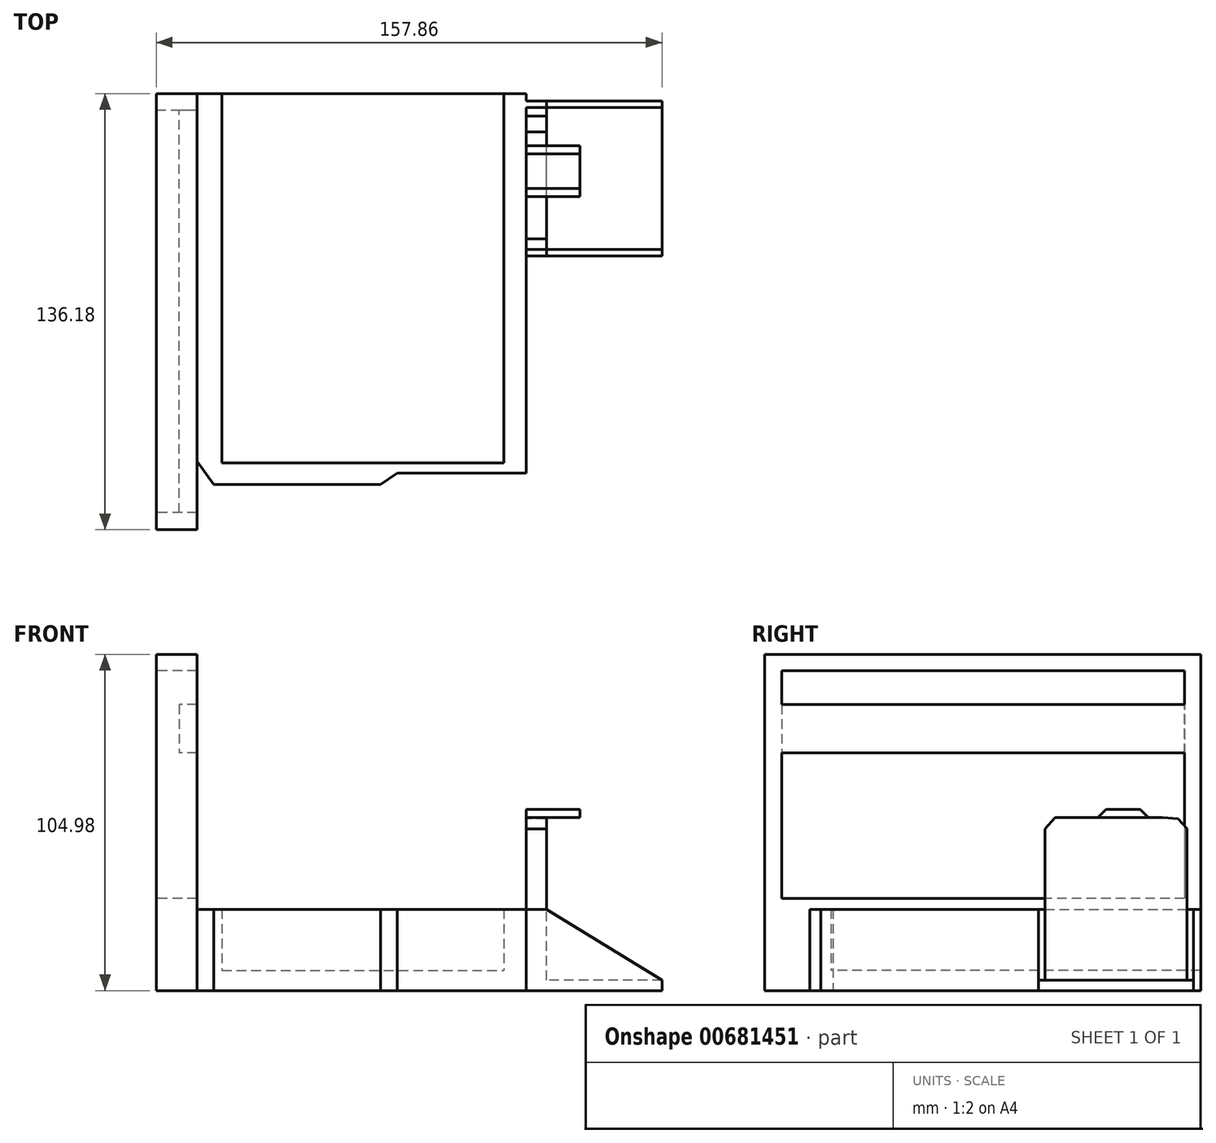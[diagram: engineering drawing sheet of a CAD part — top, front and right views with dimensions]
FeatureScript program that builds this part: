
annotation { "Feature Type Name" : "Feature", "Feature Type Description" : "" }
export const myFeature = defineFeature(function(context is Context, id is Id, definition is map)
    precondition{}
    {
        {
            var Q0;
            Q0=qCreatedBy(makeId("Top.planeOp"),FACE);
            var sketch = newSketch(context, id + "F0", { "sketchPlane" : qUnion([Q0])});
            skLineSegment(sketch, "E0.bottom", {"start": v(-45.04, 54.54) * mm, "end": v(43.03, 54.54) * mm});
            skLineSegment(sketch, "E0.top", {"start": v(-45.04, -60.87) * mm, "end": v(43.03, -60.87) * mm});
            skLineSegment(sketch, "E0.left", {"start": v(-45.04, 54.54) * mm, "end": v(-45.04, -60.87) * mm});
            skLineSegment(sketch, "E0.right", {"start": v(43.03, 54.54) * mm, "end": v(43.03, -60.87) * mm});
            skLineSegment(sketch, "E1", {"start": v(-45.04, 54.54) * mm, "end": v(-52.81, 54.54) * mm});
            skLineSegment(sketch, "E2", {"start": v(-52.81, 54.54) * mm, "end": v(-52.81, -60.3) * mm});
            skLineSegment(sketch, "E3", {"start": v(-52.81, -60.3) * mm, "end": v(-47.63, -67.5) * mm});
            skLineSegment(sketch, "E4", {"start": v(-47.63, -67.5) * mm, "end": v(4.46, -67.5) * mm});
            skLineSegment(sketch, "E5", {"start": v(4.46, -67.5) * mm, "end": v(9.64, -64.04) * mm});
            skLineSegment(sketch, "E6", {"start": v(9.64, -64.04) * mm, "end": v(49.93, -64.04) * mm});
            skLineSegment(sketch, "E7", {"start": v(49.93, -64.04) * mm, "end": v(49.93, 54.54) * mm});
            skLineSegment(sketch, "E8", {"start": v(49.93, 54.54) * mm, "end": v(43.03, 54.54) * mm});
            skSolve(sketch);
        }
        {
            var Q0;
            Q0=makeQuery(id+"F0.imprint","IMPRINT",FACE,{"disambiguationData":[TD([[makeQuery(id+"F0.imprint","IMPRINT",EDGE,{"derivedFrom":sQuery(id+"F0.wireOp",EDGE,"E0.bottom")}),-1.0]])]});
            extrude(context, id + "F1", {"entities" : qUnion([Q0]), "depth" : 6.35 * mm, "offsetDistance" : 25.4 * mm});
        }
        {
            var Q0;
            Q0=makeQuery(id+"F0.imprint","IMPRINT",FACE,{"disambiguationData":[TD([[makeQuery(id+"F0.imprint","IMPRINT",EDGE,{"derivedFrom":sQuery(id+"F0.wireOp",EDGE,"E0.top")}),-1.0]])]});
            extrude(context, id + "F2", {"entities" : qUnion([Q0]), "operationType" : NewBodyOperationType.ADD, "depth" : 25.4 * mm, "offsetDistance" : 25.4 * mm});
        }
        {
            var Q0;
            Q0=makeQuery(id+"F2.opExtrude","SWEPT_FACE",FACE,{"disambiguationData":[OSD([sQuery(id+"F0.wireOp",EDGE,"E7")])]});
            var sketch = newSketch(context, id + "F3", { "sketchPlane" : qUnion([Q0])});
            skLineSegment(sketch, "E9", {"start": v(50.24, 0) * mm, "end": v(5.83, 0) * mm});
            skLineSegment(sketch, "E10", {"start": v(5.83, 0) * mm, "end": v(5.83, 50.54) * mm});
            skLineSegment(sketch, "E11", {"start": v(5.83, 50.54) * mm, "end": v(9.1, 54.04) * mm});
            skLineSegment(sketch, "E12", {"start": v(9.1, 54.04) * mm, "end": v(42.62, 54.04) * mm});
            skLineSegment(sketch, "E13", {"start": v(42.62, 54.04) * mm, "end": v(45.76, 51.99) * mm});
            skLineSegment(sketch, "E14", {"start": v(50.24, 0) * mm, "end": v(50.24, 50.66) * mm});
            skLineSegment(sketch, "E15", {"start": v(50.24, 50.66) * mm, "end": v(47.46, 53.68) * mm});
            skLineSegment(sketch, "E16", {"start": v(47.46, 53.68) * mm, "end": v(42.62, 54.04) * mm});
            skSolve(sketch);
        }
        {
            var Q0;
            {var subQ0=sQuery(id+"F3.wireOp",EDGE,"E9");Q0=makeQuery(id+"F3.imprint","IMPRINT",FACE,{"disambiguationData":[TD([[makeQuery(id+"F3.imprint","IMPRINT",EDGE,{"derivedFrom":subQ0}),1.0]])]});}
            var Q1;
            {var subQ6=sQuery(id+"F3.wireOp",EDGE,"E11");Q1=makeQuery(id+"F3.imprint","IMPRINT",FACE,{"disambiguationData":[TD([[makeQuery(id+"F3.imprint","IMPRINT",EDGE,{"derivedFrom":subQ6}),-1.0]])]});}
            extrude(context, id + "F4", {"entities" : qUnion([Q0, Q1]), "operationType" : NewBodyOperationType.ADD, "depth" : 6.35 * mm, "offsetDistance" : 25.4 * mm});
        }
        {
            var Q0;
            Q0=makeQuery(id+"F4.opExtrude","CAP_FACE",FACE,{"disambiguationData":[OSD([sQuery(id+"F3.wireOp",EDGE,"E9"),sQuery(id+"F3.wireOp",EDGE,"E10"),sQuery(id+"F3.wireOp",EDGE,"E11"),sQuery(id+"F3.wireOp",EDGE,"E12"),sQuery(id+"F3.wireOp",EDGE,"E14"),sQuery(id+"F3.wireOp",EDGE,"E15"),sQuery(id+"F3.wireOp",EDGE,"E16")])],"isStart":false});
            var sketch = newSketch(context, id + "F5", { "sketchPlane" : qUnion([Q0])});
            skLineSegment(sketch, "E17.bottom", {"start": v(5.83, 0) * mm, "end": v(50.24, 0) * mm});
            skLineSegment(sketch, "E17.top", {"start": v(5.83, 3.25) * mm, "end": v(50.24, 3.25) * mm});
            skLineSegment(sketch, "E17.left", {"start": v(5.83, 0) * mm, "end": v(5.83, 3.25) * mm});
            skLineSegment(sketch, "E17.right", {"start": v(50.24, 0) * mm, "end": v(50.24, 3.25) * mm});
            skSolve(sketch);
        }
        {
            var Q0;
            Q0=makeQuery(id+"F5.imprint","IMPRINT",FACE,{"disambiguationData":[TD([[makeQuery(id+"F5.imprint","IMPRINT",EDGE,{"derivedFrom":sQuery(id+"F5.wireOp",EDGE,"E17.bottom")}),1.0]])]});
            extrude(context, id + "F6", {"entities" : qUnion([Q0]), "operationType" : NewBodyOperationType.ADD, "depth" : 36.07 * mm, "offsetDistance" : 25.4 * mm});
        }
        {
            var Q0;
            Q0=makeQuery(id+"F6.boolean.opBoolean","MERGE",FACE,{"derivedFrom":[makeQuery(id+"F4.opExtrude","SWEPT_FACE",FACE,{"disambiguationData":[OSD([sQuery(id+"F3.wireOp",EDGE,"E14")])]}),makeQuery(id+"F6.opExtrude","SWEPT_FACE",FACE,{"disambiguationData":[OSD([sQuery(id+"F5.wireOp",EDGE,"E17.right")])]})]});
            var sketch = newSketch(context, id + "F7", { "sketchPlane" : qUnion([Q0])});
            skLineSegment(sketch, "E18", {"start": v(-49.8, 25.4) * mm, "end": v(-56.34, 25.4) * mm});
            skLineSegment(sketch, "E19", {"start": v(-56.34, 25.4) * mm, "end": v(-92.35, 3.25) * mm});
            skLineSegment(sketch, "E20", {"start": v(-92.35, 3.25) * mm, "end": v(-92.35, 0) * mm});
            skLineSegment(sketch, "E21", {"start": v(-92.35, 0) * mm, "end": v(-49.93, 0) * mm});
            skLineSegment(sketch, "E22", {"start": v(-49.93, 0) * mm, "end": v(-49.8, 25.4) * mm});
            skSolve(sketch);
        }
        {
            var Q0;
            Q0=makeQuery(id+"F7.imprint","IMPRINT",FACE,{"disambiguationData":[TD([[makeQuery(id+"F7.imprint","IMPRINT",EDGE,{"derivedFrom":sQuery(id+"F7.wireOp",EDGE,"E20")}),-1.0]])]});
            var Q1;
            {var subQ0=sQuery(id+"F7.wireOp",EDGE,"E19");Q1=makeQuery(id+"F7.imprint","IMPRINT",FACE,{"disambiguationData":[TD([[makeQuery(id+"F7.imprint","IMPRINT",EDGE,{"derivedFrom":subQ0}),1.0]])]});}
            extrude(context, id + "F8", {"entities" : qUnion([Q0, Q1]), "operationType" : NewBodyOperationType.ADD, "depth" : 2.03 * mm, "offsetDistance" : 25.4 * mm});
        }
        {
            var Q0;
            Q0=makeQuery(id+"F6.boolean.opBoolean","MERGE",FACE,{"derivedFrom":[makeQuery(id+"F4.opExtrude","SWEPT_FACE",FACE,{"disambiguationData":[OSD([sQuery(id+"F3.wireOp",EDGE,"E10")])]}),makeQuery(id+"F6.opExtrude","SWEPT_FACE",FACE,{"disambiguationData":[OSD([sQuery(id+"F5.wireOp",EDGE,"E17.left")])]})]});
            var sketch = newSketch(context, id + "F9", { "sketchPlane" : qUnion([Q0])});
            skLineSegment(sketch, "E23", {"start": v(56.28, 25.33) * mm, "end": v(92.35, 3.25) * mm});
            skLineSegment(sketch, "E24", {"start": v(92.35, 3.25) * mm, "end": v(92.35, 0) * mm});
            skLineSegment(sketch, "E25", {"start": v(92.35, 0) * mm, "end": v(49.93, 0) * mm});
            skLineSegment(sketch, "E26", {"start": v(49.93, 0) * mm, "end": v(49.93, 25.4) * mm});
            skLineSegment(sketch, "E27", {"start": v(49.93, 25.4) * mm, "end": v(56.28, 25.33) * mm});
            skSolve(sketch);
        }
        {
            var Q0;
            {var subQ0=sQuery(id+"F9.wireOp",EDGE,"E23");Q0=makeQuery(id+"F9.imprint","IMPRINT",FACE,{"disambiguationData":[TD([[makeQuery(id+"F9.imprint","IMPRINT",EDGE,{"derivedFrom":subQ0}),-1.0]])]});}
            var Q1;
            Q1=makeQuery(id+"F9.imprint","IMPRINT",FACE,{"disambiguationData":[TD([[makeQuery(id+"F9.imprint","IMPRINT",EDGE,{"derivedFrom":sQuery(id+"F9.wireOp",EDGE,"E24")}),1.0]])]});
            extrude(context, id + "F10", {"entities" : qUnion([Q0, Q1]), "operationType" : NewBodyOperationType.ADD, "depth" : 2.03 * mm, "offsetDistance" : 25.4 * mm});
        }
        {
            var Q0;
            Q0=makeQuery(id+"F4.opExtrude","SWEPT_FACE",FACE,{"disambiguationData":[OSD([sQuery(id+"F3.wireOp",EDGE,"E12")])]});
            var sketch = newSketch(context, id + "F11", { "sketchPlane" : qUnion([Q0])});
            skLineSegment(sketch, "E28.bottom", {"start": v(49.93, 38.2) * mm, "end": v(66.7, 38.2) * mm});
            skLineSegment(sketch, "E28.top", {"start": v(49.93, 22.42) * mm, "end": v(66.7, 22.42) * mm});
            skLineSegment(sketch, "E28.left", {"start": v(49.93, 38.2) * mm, "end": v(49.93, 22.42) * mm});
            skLineSegment(sketch, "E28.right", {"start": v(66.7, 38.2) * mm, "end": v(66.7, 22.42) * mm});
            skSolve(sketch);
        }
        {
            var Q0;
            {var subQ0=sQuery(id+"F11.wireOp",EDGE,"E28.right");Q0=makeQuery(id+"F11.imprint","IMPRINT",FACE,{"disambiguationData":[TD([[makeQuery(id+"F11.imprint","IMPRINT",EDGE,{"derivedFrom":subQ0}),-1.0]])]});}
            var Q1;
            {var subQ0=sQuery(id+"F11.wireOp",EDGE,"E28.left");Q1=makeQuery(id+"F11.imprint","IMPRINT",FACE,{"disambiguationData":[TD([[makeQuery(id+"F11.imprint","IMPRINT",EDGE,{"derivedFrom":subQ0}),-1.0]])]});}
            extrude(context, id + "F12", {"entities" : qUnion([Q0, Q1]), "operationType" : NewBodyOperationType.ADD, "depth" : 2.54 * mm, "offsetDistance" : 25.4 * mm});
        }
        {
            var Q0;
            Q0=makeQuery(id+"F12.opExtrude","CAP_EDGE",EDGE,{"disambiguationData":[OSD([sQuery(id+"F11.wireOp",EDGE,"E28.bottom")])],"isStart":false});
            chamfer(context, id + "F13", {"entities" : qUnion([Q0]), "width" : 2.54 * mm, "tangentPropagation" : true});
        }
        {
            var Q0;
            Q0=makeQuery(id+"F12.opExtrude","CAP_EDGE",EDGE,{"disambiguationData":[OSD([sQuery(id+"F11.wireOp",EDGE,"E28.top")])],"isStart":false});
            chamfer(context, id + "F14", {"entities" : qUnion([Q0]), "width" : 2.54 * mm, "tangentPropagation" : true});
        }
        {
            var Q0;
            Q0=makeQuery(id+"F2.opExtrude","SWEPT_FACE",FACE,{"disambiguationData":[OSD([sQuery(id+"F0.wireOp",EDGE,"E2")])]});
            var sketch = newSketch(context, id + "F15", { "sketchPlane" : qUnion([Q0])});
            skLineSegment(sketch, "E29.bottom", {"start": v(-54.54, 0) * mm, "end": v(81.64, 0) * mm});
            skLineSegment(sketch, "E29.top", {"start": v(-54.54, 28.78) * mm, "end": v(81.64, 28.78) * mm});
            skLineSegment(sketch, "E29.left", {"start": v(-54.54, 0) * mm, "end": v(-54.54, 28.78) * mm});
            skLineSegment(sketch, "E29.right", {"start": v(81.64, 0) * mm, "end": v(81.64, 28.78) * mm});
            skSolve(sketch);
        }
        {
            var Q0;
            Q0 = qSketchRegion(id + "F15", true);
            extrude(context, id + "F16", {"entities" : qUnion([Q0]), "operationType" : NewBodyOperationType.ADD, "depth" : 12.7 * mm, "offsetDistance" : 25.4 * mm});
        }
        {
            var Q0;
            Q0=makeQuery(id+"F16.opExtrude","SWEPT_FACE",FACE,{"disambiguationData":[OSD([sQuery(id+"F15.wireOp",EDGE,"E29.top")])]});
            var sketch = newSketch(context, id + "F17", { "sketchPlane" : qUnion([Q0])});
            skLineSegment(sketch, "E30", {"start": v(-52.81, 54.54) * mm, "end": v(-65.51, 54.54) * mm});
            skLineSegment(sketch, "E31", {"start": v(-65.51, 54.54) * mm, "end": v(-65.51, 49.44) * mm});
            skLineSegment(sketch, "E32", {"start": v(-65.51, 49.44) * mm, "end": v(-52.81, 49.44) * mm});
            skLineSegment(sketch, "E33", {"start": v(-52.81, 49.44) * mm, "end": v(-52.81, 54.54) * mm});
            skSolve(sketch);
        }
        {
            var Q0;
            Q0=makeQuery(id+"F17.imprint","IMPRINT",FACE,{"disambiguationData":[TD([[makeQuery(id+"F17.imprint","IMPRINT",EDGE,{"derivedFrom":sQuery(id+"F17.wireOp",EDGE,"E30")}),-1.0]])]});
            extrude(context, id + "F18", {"entities" : qUnion([Q0]), "operationType" : NewBodyOperationType.ADD, "depth" : 76.2 * mm, "offsetDistance" : 25.4 * mm});
        }
        {
            var Q0;
            Q0=makeQuery(id+"F16.opExtrude","SWEPT_FACE",FACE,{"disambiguationData":[OSD([sQuery(id+"F15.wireOp",EDGE,"E29.top")])]});
            var sketch = newSketch(context, id + "F19", { "sketchPlane" : qUnion([Q0])});
            skLineSegment(sketch, "E34.bottom", {"start": v(-52.81, -81.64) * mm, "end": v(-65.51, -81.64) * mm});
            skLineSegment(sketch, "E34.top", {"start": v(-52.81, -76.35) * mm, "end": v(-65.51, -76.35) * mm});
            skLineSegment(sketch, "E34.left", {"start": v(-52.81, -81.64) * mm, "end": v(-52.81, -76.35) * mm});
            skLineSegment(sketch, "E34.right", {"start": v(-65.51, -81.64) * mm, "end": v(-65.51, -76.35) * mm});
            skSolve(sketch);
        }
        {
            var Q0;
            Q0=makeQuery(id+"F19.imprint","IMPRINT",FACE,{"disambiguationData":[TD([[makeQuery(id+"F19.imprint","IMPRINT",EDGE,{"derivedFrom":sQuery(id+"F19.wireOp",EDGE,"E34.bottom")}),1.0]])]});
            extrude(context, id + "F20", {"entities" : qUnion([Q0]), "operationType" : NewBodyOperationType.ADD, "depth" : 76.2 * mm, "offsetDistance" : 25.4 * mm});
        }
        {
            var Q0;
            Q0=makeQuery(id+"F18.opExtrude","SWEPT_FACE",FACE,{"disambiguationData":[OSD([sQuery(id+"F17.wireOp",EDGE,"E32")])]});
            var sketch = newSketch(context, id + "F21", { "sketchPlane" : qUnion([Q0])});
            skLineSegment(sketch, "E35.bottom", {"start": v(-65.51, 104.98) * mm, "end": v(-52.81, 104.98) * mm});
            skLineSegment(sketch, "E35.top", {"start": v(-65.51, 99.88) * mm, "end": v(-52.81, 99.88) * mm});
            skLineSegment(sketch, "E35.left", {"start": v(-65.51, 104.98) * mm, "end": v(-65.51, 99.88) * mm});
            skLineSegment(sketch, "E35.right", {"start": v(-52.81, 104.98) * mm, "end": v(-52.81, 99.88) * mm});
            skSolve(sketch);
        }
        {
            var Q0;
            Q0=makeQuery(id+"F21.imprint","IMPRINT",FACE,{"disambiguationData":[TD([[makeQuery(id+"F21.imprint","IMPRINT",EDGE,{"derivedFrom":sQuery(id+"F21.wireOp",EDGE,"E35.bottom")}),-1.0]])]});
            extrude(context, id + "F22", {"entities" : qUnion([Q0]), "operationType" : NewBodyOperationType.ADD, "depth" : 127.76 * mm, "offsetDistance" : 25.4 * mm});
        }
        {
            var Q0;
            Q0=makeQuery(id+"F18.opExtrude","SWEPT_FACE",FACE,{"disambiguationData":[OSD([sQuery(id+"F17.wireOp",EDGE,"E32")])]});
            var sketch = newSketch(context, id + "F23", { "sketchPlane" : qUnion([Q0])});
            skLineSegment(sketch, "E36.bottom", {"start": v(-58.4, 74.22) * mm, "end": v(-52.81, 74.22) * mm});
            skLineSegment(sketch, "E36.top", {"start": v(-58.4, 89.34) * mm, "end": v(-52.81, 89.34) * mm});
            skLineSegment(sketch, "E36.left", {"start": v(-58.4, 74.22) * mm, "end": v(-58.4, 89.34) * mm});
            skLineSegment(sketch, "E36.right", {"start": v(-52.81, 74.22) * mm, "end": v(-52.81, 89.34) * mm});
            skSolve(sketch);
        }
        {
            var Q0;
            Q0=makeQuery(id+"F23.imprint","IMPRINT",FACE,{"disambiguationData":[TD([[makeQuery(id+"F23.imprint","IMPRINT",EDGE,{"derivedFrom":sQuery(id+"F23.wireOp",EDGE,"E36.bottom")}),1.0]])]});
            extrude(context, id + "F24", {"entities" : qUnion([Q0]), "operationType" : NewBodyOperationType.ADD, "depth" : 128.27 * mm, "offsetDistance" : 25.4 * mm});
        }
    });
